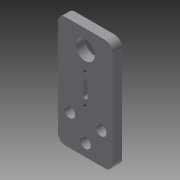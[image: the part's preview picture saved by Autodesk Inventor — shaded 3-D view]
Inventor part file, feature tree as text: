
AUTODESK INVENTOR PART (.ipt)
format: ipt  version: 2015 SP1 (Build 190203100, 203)  size: 124,416 bytes
history: native  units: in
note: dims shown in document units (in); Inventor stores cm internally (conversion verified against a paired STEP export)
features: sketch x1, extrude x1, hole x1, fillet x1
ambient origin geometry x8: Origin, YZ Plane, XZ Plane, XY Plane, X Axis, Y Axis, Z Axis, Center Point
bodies: Body1 (feature_tree)
feature tree (4):
  sketch  "Sketch1"  dims[d3=1.378in d4=0.2756in d6=0.2756in d7=0.2756in d12=0.4724in d13=0.4724in d25=0.0968in d26=0.2362in d27=0.119in d28=0.0787in d29=0.5635in d30=0.3465in d31=0.8108in d36=0.0591in d37=0.315in d38=0.748in d39=0.4724in d40=0.4724in d41=0.315in d42=0.315in d43=0.7874in d44=0.2362in d45=0.0in d46=0.1969in]
  extrude  "Extrusion4"  Depth=0.1969in
  hole  "Hole1"  [1 undecoded]
  fillet  "Fillet3"  Radius=0.2756in
note: 1 required parameter value undecoded (feature->parameter linkage not recoverable at this tier; creation-order binding heuristic only, values carry confidence <= 0.55)
